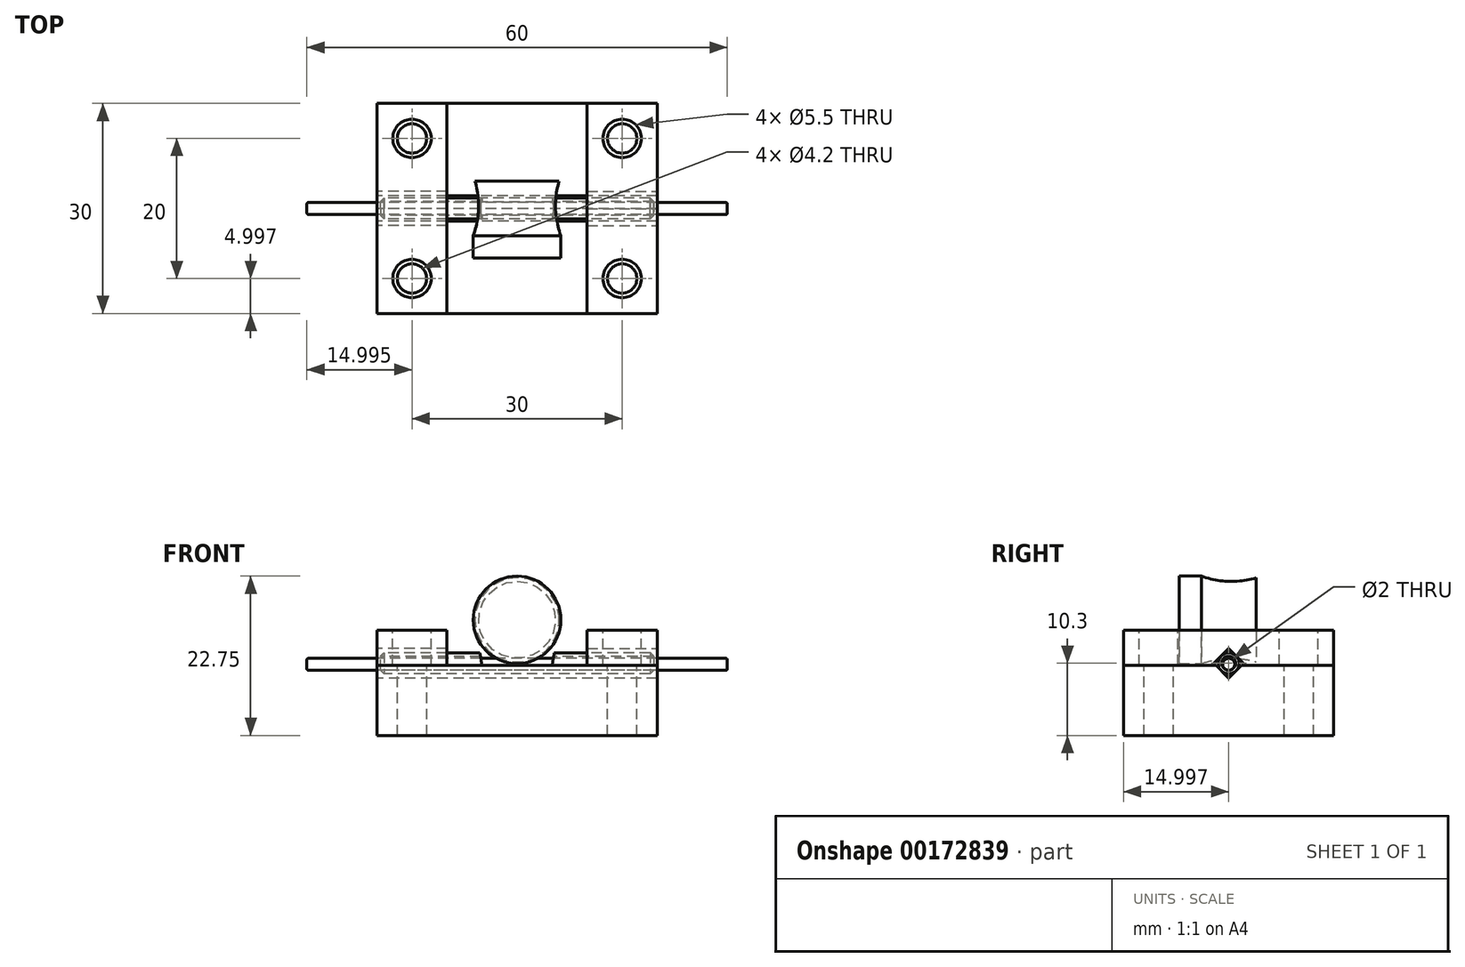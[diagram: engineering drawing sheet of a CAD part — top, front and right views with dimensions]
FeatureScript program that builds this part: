
annotation { "Feature Type Name" : "Feature", "Feature Type Description" : "" }
export const myFeature = defineFeature(function(context is Context, id is Id, definition is map)
    precondition{}
    {
        {
            var Q0;
            Q0=qCreatedBy(makeId("Top.planeOp"),FACE);
            var sketch = newSketch(context, id + "F0", { "sketchPlane" : qUnion([Q0])});
            skLineSegment(sketch, "E0.bottom", {"start": v(4.07, 8.16) * mm, "end": v(44.07, 8.16) * mm});
            skLineSegment(sketch, "E0.top", {"start": v(4.07, -21.84) * mm, "end": v(44.07, -21.84) * mm});
            skLineSegment(sketch, "E0.left", {"start": v(4.07, 8.16) * mm, "end": v(4.07, -21.84) * mm});
            skLineSegment(sketch, "E0.right", {"start": v(44.07, 8.16) * mm, "end": v(44.07, -21.84) * mm});
            skPoint(sketch, "E1", {"position": v(9.07, 3.16) * mm});
            skPoint(sketch, "E2", {"position": v(39.07, -16.84) * mm});
            skPoint(sketch, "E3", {"position": v(9.07, -16.84) * mm});
            skPoint(sketch, "E4", {"position": v(39.07, 3.16) * mm});
            skSolve(sketch);
        }
        {
            var Q0;
            Q0=makeQuery(id+"F0.imprint","IMPRINT",FACE,{"disambiguationData":[TD([[makeQuery(id+"F0.imprint","IMPRINT",EDGE,{"derivedFrom":sQuery(id+"F0.wireOp",EDGE,"E0.bottom")}),-1.0]])]});
            extrude(context, id + "F1", {"entities" : qUnion([Q0]), "depth" : 10 * mm});
        }
        {
            var Q0;
            Q0=makeQuery(id+"F1.opExtrude","CAP_FACE",FACE,{"disambiguationData":[OSD([sQuery(id+"F0.wireOp",EDGE,"E0.bottom"),sQuery(id+"F0.wireOp",EDGE,"E0.top"),sQuery(id+"F0.wireOp",EDGE,"E0.left"),sQuery(id+"F0.wireOp",EDGE,"E0.right")])],"isStart":false});
            var sketch = newSketch(context, id + "F2", { "sketchPlane" : qUnion([Q0])});
            skPoint(sketch, "E5", {"position": v(9.07, 3.16) * mm});
            skPoint(sketch, "E6", {"position": v(39.07, -16.84) * mm});
            skPoint(sketch, "E7", {"position": v(39.07, 3.16) * mm});
            skPoint(sketch, "E8", {"position": v(9.07, -16.84) * mm});
            skSolve(sketch);
        }
        {
            var Q0;
            Q0=makeQuery(id+"F1.opExtrude","SWEPT_FACE",FACE,{"disambiguationData":[OSD([sQuery(id+"F0.wireOp",EDGE,"E0.left")])]});
            var sketch = newSketch(context, id + "F3", { "sketchPlane" : qUnion([Q0])});
            skLineSegment(sketch, "E9", {"start": v(5.02, 10) * mm, "end": v(6.84, 8.18) * mm});
            skLineSegment(sketch, "E10", {"start": v(6.84, 8.18) * mm, "end": v(8.66, 10) * mm});
            skPoint(sketch, "E11", {"position": v(6.84, 10) * mm});
            skLineSegment(sketch, "E12", {"start": v(5.02, 10) * mm, "end": v(6.84, 10) * mm});
            skLineSegment(sketch, "E13", {"start": v(6.84, 10) * mm, "end": v(8.66, 10) * mm});
            skCircle(sketch, "E14", {"center": v(6.84, 10.3) * mm, "radius": 1.5 * mm});
            skLineSegment(sketch, "E15", {"start": v(5.34, 10.3) * mm, "end": v(8.34, 10.3) * mm});
            skSolve(sketch);
        }
        {
            var Q0;
            {var subQ0=sQuery(id+"F3.wireOp",EDGE,"E10");var subQ1=sQuery(id+"F3.wireOp",EDGE,"E9");var subQ2=makeQuery(id+"F3.imprint","INTERSECT",VERTEX,{"derivedFrom":[subQ1,subQ0]});Q0=makeQuery(id+"F3.imprint","IMPRINT",FACE,{"disambiguationData":[TD([[makeQuery(id+"F3.imprint","IMPRINT",EDGE,{"disambiguationData":[TD([[subQ2,1.0]])],"derivedFrom":subQ1}),1.0]])]});}
            var Q1;
            {var subQ3=sQuery(id+"F3.wireOp",EDGE,"E12");var subQ5=sQuery(id+"F3.wireOp",EDGE,"E13");var subQ6=makeQuery(id+"F3.imprint","INTERSECT",VERTEX,{"derivedFrom":[subQ3,subQ5]});Q1=makeQuery(id+"F3.imprint","IMPRINT",FACE,{"disambiguationData":[TD([[makeQuery(id+"F3.imprint","IMPRINT",EDGE,{"disambiguationData":[TD([[subQ6,1.0]])],"derivedFrom":subQ3}),-1.0]])]});}
            var Q2;
            {var subQ0=sQuery(id+"F3.wireOp",EDGE,"E12");var subQ3=sQuery(id+"F3.wireOp",EDGE,"E14");var subQ5=makeQuery(id+"F3.imprint","INTERSECT",VERTEX,{"derivedFrom":[subQ0,subQ3]});Q2=makeQuery(id+"F3.imprint","IMPRINT",FACE,{"disambiguationData":[TD([[makeQuery(id+"F3.imprint","IMPRINT",EDGE,{"disambiguationData":[TD([[subQ5,-1.0]])],"derivedFrom":subQ3}),-1.0]])]});}
            var Q3;
            {var subQ0=sQuery(id+"F3.wireOp",EDGE,"E13");var subQ3=sQuery(id+"F3.wireOp",EDGE,"E14");var subQ5=makeQuery(id+"F3.imprint","INTERSECT",VERTEX,{"derivedFrom":[subQ0,subQ3]});Q3=makeQuery(id+"F3.imprint","IMPRINT",FACE,{"disambiguationData":[TD([[makeQuery(id+"F3.imprint","IMPRINT",EDGE,{"disambiguationData":[TD([[subQ5,1.0]])],"derivedFrom":subQ3}),-1.0]])]});}
            extrude(context, id + "F4", {"entities" : qUnion([Q0, Q1, Q2, Q3]), "operationType" : NewBodyOperationType.REMOVE, "endBound" : BoundingType.UP_TO_NEXT, "oppositeDirection" : true, "depth" : 25 * mm});
        }
        {
            var Q0;
            Q0=sQuery(id+"F2.wireOp",VERTEX,"E5");
            var Q1;
            Q1=sQuery(id+"F2.wireOp",VERTEX,"E7");
            var Q2;
            Q2=sQuery(id+"F2.wireOp",VERTEX,"E6");
            var Q3;
            Q3=sQuery(id+"F2.wireOp",VERTEX,"E8");
            var Q4;
            Q4=makeQuery(id+"F1.opExtrude","SWEPT_BODY",BODY,{"disambiguationData":[OSD([sQuery(id+"F0.wireOp",EDGE,"E0.bottom"),sQuery(id+"F0.wireOp",EDGE,"E0.top"),sQuery(id+"F0.wireOp",EDGE,"E0.left"),sQuery(id+"F0.wireOp",EDGE,"E0.right")])]});
            hole(context, id + "F5", {"style" : HoleStyle.SIMPLE, "endStyle" : HoleEndStyle.THROUGH, "standardTappedOrClearance" : lookupTablePath({ "standard" : "ISO", "engagement" : "75%", "pitch" : "0.8 mm", "size" : "M5", "type" : "Tapped" }), "standardBlindInLast" : lookupTablePath({ "standard" : "ISO", "engagement" : "75%", "pitch" : "0.8 mm", "size" : "M5", "type" : "Tapped" }), "holeDiameter" : 4.2 * mm, "locations" : qUnion([Q0, Q1, Q2, Q3]), "scope" : qUnion([Q4]), "isTappedThrough" : true, "majorDiameter" : 5 * mm, "showTappedDepth" : true});
        }
        {
            var Q0;
            Q0=makeQuery(id+"F1.opExtrude","SWEPT_FACE",FACE,{"disambiguationData":[OSD([sQuery(id+"F0.wireOp",EDGE,"E0.left")])]});
            var sketch = newSketch(context, id + "F6", { "sketchPlane" : qUnion([Q0])});
            skLineSegment(sketch, "E16.bottom", {"start": v(-8.16, 10) * mm, "end": v(21.84, 10) * mm});
            skLineSegment(sketch, "E16.top", {"start": v(-8.16, 15) * mm, "end": v(21.84, 15) * mm});
            skLineSegment(sketch, "E16.left", {"start": v(-8.16, 10) * mm, "end": v(-8.16, 15) * mm});
            skLineSegment(sketch, "E16.right", {"start": v(21.84, 10) * mm, "end": v(21.84, 15) * mm});
            skCircle(sketch, "E17", {"center": v(6.84, 10.3) * mm, "radius": 1.5 * mm});
            skLineSegment(sketch, "E18", {"start": v(4.42, 10) * mm, "end": v(6.84, 12.42) * mm});
            skLineSegment(sketch, "E19", {"start": v(6.84, 12.42) * mm, "end": v(9.26, 10) * mm});
            skSolve(sketch);
        }
        {
            var Q0;
            Q0=makeQuery(id+"F6.imprint","IMPRINT",FACE,{"disambiguationData":[TD([[makeQuery(id+"F6.imprint","IMPRINT",EDGE,{"derivedFrom":sQuery(id+"F6.wireOp",EDGE,"E16.top")}),-1.0]])]});
            extrude(context, id + "F7", {"entities" : qUnion([Q0]), "oppositeDirection" : true, "depth" : 10 * mm});
        }
        {
            var Q0;
            Q0=makeQuery(id+"F1.opExtrude","SWEPT_FACE",FACE,{"disambiguationData":[OSD([sQuery(id+"F0.wireOp",EDGE,"E0.right")])]});
            var sketch = newSketch(context, id + "F8", { "sketchPlane" : qUnion([Q0])});
            skCircle(sketch, "E20", {"center": v(-6.84, 10.3) * mm, "radius": 1.5 * mm});
            skLineSegment(sketch, "E21", {"start": v(-9.26, 10) * mm, "end": v(-6.84, 12.42) * mm});
            skLineSegment(sketch, "E22", {"start": v(-6.84, 12.42) * mm, "end": v(-4.42, 10) * mm});
            skLineSegment(sketch, "E23.bottom", {"start": v(-21.84, 10) * mm, "end": v(8.16, 10) * mm});
            skLineSegment(sketch, "E23.top", {"start": v(-21.84, 15) * mm, "end": v(8.16, 15) * mm});
            skLineSegment(sketch, "E23.left", {"start": v(-21.84, 10) * mm, "end": v(-21.84, 15) * mm});
            skLineSegment(sketch, "E23.right", {"start": v(8.16, 10) * mm, "end": v(8.16, 15) * mm});
            skSolve(sketch);
        }
        {
            var Q0;
            Q0=makeQuery(id+"F8.imprint","IMPRINT",FACE,{"disambiguationData":[TD([[makeQuery(id+"F8.imprint","IMPRINT",EDGE,{"derivedFrom":sQuery(id+"F8.wireOp",EDGE,"E23.top")}),-1.0]])]});
            extrude(context, id + "F9", {"entities" : qUnion([Q0]), "oppositeDirection" : true, "depth" : 10 * mm});
        }
        {
            var Q0;
            Q0=makeQuery(id+"F7.opExtrude","SWEPT_FACE",FACE,{"disambiguationData":[OSD([sQuery(id+"F6.wireOp",EDGE,"E16.top")])]});
            var sketch = newSketch(context, id + "F10", { "sketchPlane" : qUnion([Q0])});
            skPoint(sketch, "E24", {"position": v(9.07, 3.16) * mm});
            skPoint(sketch, "E25", {"position": v(9.07, -16.84) * mm});
            skCircle(sketch, "E26", {"center": v(9.07, 3.16) * mm, "radius": 2.75 * mm});
            skCircle(sketch, "E27", {"center": v(9.07, -16.84) * mm, "radius": 2.75 * mm});
            skSolve(sketch);
        }
        {
            var Q0;
            Q0=makeQuery(id+"F10.imprint","IMPRINT",FACE,{"disambiguationData":[TD([[makeQuery(id+"F10.imprint","IMPRINT",EDGE,{"derivedFrom":sQuery(id+"F10.wireOp",EDGE,"E26")}),1.0]])]});
            var Q1;
            Q1=makeQuery(id+"F10.imprint","IMPRINT",FACE,{"disambiguationData":[TD([[makeQuery(id+"F10.imprint","IMPRINT",EDGE,{"derivedFrom":sQuery(id+"F10.wireOp",EDGE,"E27")}),1.0]])]});
            extrude(context, id + "F11", {"entities" : qUnion([Q0, Q1]), "operationType" : NewBodyOperationType.REMOVE, "endBound" : BoundingType.UP_TO_NEXT, "oppositeDirection" : true, "depth" : 25 * mm});
        }
        {
            var Q0;
            Q0=makeQuery(id+"F9.opExtrude","SWEPT_FACE",FACE,{"disambiguationData":[OSD([sQuery(id+"F8.wireOp",EDGE,"E23.top")])]});
            var sketch = newSketch(context, id + "F12", { "sketchPlane" : qUnion([Q0])});
            skCircle(sketch, "E28", {"center": v(39.07, 3.16) * mm, "radius": 2.75 * mm});
            skCircle(sketch, "E29", {"center": v(39.07, -16.84) * mm, "radius": 2.75 * mm});
            skSolve(sketch);
        }
        {
            var Q0;
            Q0=makeQuery(id+"F12.imprint","IMPRINT",FACE,{"disambiguationData":[TD([[makeQuery(id+"F12.imprint","IMPRINT",EDGE,{"derivedFrom":sQuery(id+"F12.wireOp",EDGE,"E28")}),1.0]])]});
            var Q1;
            Q1=makeQuery(id+"F12.imprint","IMPRINT",FACE,{"disambiguationData":[TD([[makeQuery(id+"F12.imprint","IMPRINT",EDGE,{"derivedFrom":sQuery(id+"F12.wireOp",EDGE,"E29")}),1.0]])]});
            extrude(context, id + "F13", {"entities" : qUnion([Q0, Q1]), "operationType" : NewBodyOperationType.REMOVE, "endBound" : BoundingType.UP_TO_NEXT, "oppositeDirection" : true, "depth" : 25 * mm});
        }
        {
            var Q0;
            Q0=makeQuery(id+"F7.opExtrude","CAP_FACE",FACE,{"disambiguationData":[OSD([sQuery(id+"F6.wireOp",EDGE,"E16.bottom"),sQuery(id+"F6.wireOp",EDGE,"E16.top"),sQuery(id+"F6.wireOp",EDGE,"E16.left"),sQuery(id+"F6.wireOp",EDGE,"E16.right"),sQuery(id+"F6.wireOp",EDGE,"E18"),sQuery(id+"F6.wireOp",EDGE,"E19")])],"isStart":true});
            cPlane(context, id + "F14", {"entities" : qUnion([Q0]), "cplaneType" : CPlaneType.OFFSET, "offset" : 0 * mm, "width" : 150 * mm, "height" : 150 * mm});
        }
        {
            var Q0;
            Q0=qCreatedBy(id+"F14.planeOp",FACE);
            var sketch = newSketch(context, id + "F15", { "sketchPlane" : qUnion([Q0])});
            skCircle(sketch, "E30", {"center": v(6.84, 10.3) * mm, "radius": 1.5 * mm});
            skCircle(sketch, "E31", {"center": v(6.84, 10.3) * mm, "radius": 1 * mm});
            skSolve(sketch);
        }
        {
            var Q0;
            Q0=makeQuery(id+"F15.imprint","IMPRINT",FACE,{"disambiguationData":[TD([[makeQuery(id+"F15.imprint","IMPRINT",EDGE,{"derivedFrom":sQuery(id+"F15.wireOp",EDGE,"E30")}),1.0]])]});
            extrude(context, id + "F16", {"entities" : qUnion([Q0]), "oppositeDirection" : true, "depth" : 40 * mm});
        }
        {
            var Q0;
            Q0=makeQuery(id+"F1.opExtrude","SWEPT_FACE",FACE,{"disambiguationData":[OSD([sQuery(id+"F0.wireOp",EDGE,"E0.top")])]});
            var sketch = newSketch(context, id + "F17", { "sketchPlane" : qUnion([Q0])});
            skPoint(sketch, "E32", {"position": v(24.07, 10) * mm});
            skLineSegment(sketch, "E33.bottom", {"start": v(19.07, 15.8) * mm, "end": v(29.07, 15.8) * mm});
            skLineSegment(sketch, "E33.top", {"start": v(19.07, 10) * mm, "end": v(29.07, 10) * mm});
            skLineSegment(sketch, "E33.left", {"start": v(19.07, 15.8) * mm, "end": v(19.07, 10) * mm});
            skLineSegment(sketch, "E33.right", {"start": v(29.07, 15.8) * mm, "end": v(29.07, 10) * mm});
            skPoint(sketch, "E34", {"position": v(24.07, 15.8) * mm});
            skLineSegment(sketch, "E35", {"start": v(19.07, 10) * mm, "end": v(18.07, 15.8) * mm});
            skLineSegment(sketch, "E36", {"start": v(18.07, 15.8) * mm, "end": v(19.07, 15.8) * mm});
            skLineSegment(sketch, "E37", {"start": v(29.07, 15.8) * mm, "end": v(30.07, 15.8) * mm});
            skLineSegment(sketch, "E38", {"start": v(30.07, 15.8) * mm, "end": v(29.07, 10) * mm});
            skSolve(sketch);
        }
        {
            var Q0;
            Q0=makeQuery(id+"F17.imprint","IMPRINT",FACE,{"disambiguationData":[TD([[makeQuery(id+"F17.imprint","IMPRINT",EDGE,{"derivedFrom":sQuery(id+"F17.wireOp",EDGE,"E33.bottom")}),-1.0]])]});
            var Q1;
            Q1=makeQuery(id+"F17.imprint","IMPRINT",FACE,{"disambiguationData":[TD([[makeQuery(id+"F17.imprint","IMPRINT",EDGE,{"derivedFrom":sQuery(id+"F17.wireOp",EDGE,"E33.left")}),-1.0]])]});
            var Q2;
            Q2=makeQuery(id+"F17.imprint","IMPRINT",FACE,{"disambiguationData":[TD([[makeQuery(id+"F17.imprint","IMPRINT",EDGE,{"derivedFrom":sQuery(id+"F17.wireOp",EDGE,"E33.right")}),1.0]])]});
            extrude(context, id + "F18", {"entities" : qUnion([Q0, Q1, Q2]), "operationType" : NewBodyOperationType.REMOVE, "oppositeDirection" : true, "depth" : 25 * mm});
        }
        {
            var Q0;
            Q0=makeQuery(id+"F16.opExtrude","CAP_EDGE",EDGE,{"disambiguationData":[OSD([sQuery(id+"F15.wireOp",EDGE,"E30")])],"isStart":true});
            var Q1;
            Q1=makeQuery(id+"F16.opExtrude","CAP_EDGE",EDGE,{"disambiguationData":[OSD([sQuery(id+"F15.wireOp",EDGE,"E30")])],"isStart":false});
            chamfer(context, id + "F19", {"entities" : qUnion([Q0, Q1]), "width" : 1 * mm, "tangentPropagation" : true});
        }
        {
            var Q0;
            Q0=qCreatedBy(id+"F14.planeOp",FACE);
            var sketch = newSketch(context, id + "F20", { "sketchPlane" : qUnion([Q0])});
            skCircle(sketch, "E39", {"center": v(6.84, 10.15) * mm, "radius": 0.85 * mm});
            skSolve(sketch);
        }
        {
            var Q0;
            Q0=makeQuery(id+"F20.imprint","IMPRINT",FACE,{"disambiguationData":[TD([[makeQuery(id+"F20.imprint","IMPRINT",EDGE,{"derivedFrom":sQuery(id+"F20.wireOp",EDGE,"E39")}),1.0]])]});
            extrude(context, id + "F21", {"entities" : qUnion([Q0]), "oppositeDirection" : true, "depth" : 50 * mm});
        }
        {
            var Q0;
            Q0=makeQuery(id+"F21.opExtrude","CAP_FACE",FACE,{"disambiguationData":[OSD([sQuery(id+"F20.wireOp",EDGE,"E39")])],"isStart":true});
            extrude(context, id + "F22", {"entities" : qUnion([Q0]), "operationType" : NewBodyOperationType.ADD, "depth" : 10 * mm});
        }
        {
            var Q0;
            Q0=makeQuery(id+"F1.opExtrude","SWEPT_FACE",FACE,{"disambiguationData":[OSD([sQuery(id+"F0.wireOp",EDGE,"E0.left")])]});
            cPlane(context, id + "F23", {"entities" : qUnion([Q0]), "cplaneType" : CPlaneType.OFFSET, "offset" : 20 * mm, "oppositeDirection" : true, "width" : 150 * mm, "height" : 150 * mm});
        }
        {
            var Q0;
            Q0=qCreatedBy(id+"F23.planeOp",FACE);
            var sketch = newSketch(context, id + "F24", { "sketchPlane" : qUnion([Q0])});
            skLineSegment(sketch, "E40", {"start": v(13.92, 22.75) * mm, "end": v(10.72, 22.75) * mm});
            skArc(sketch, "E41", {"start": v(2.92, 22.5) * mm, "mid": v(6.84, 22) * mm, "end": v(10.72, 22.75) * mm});
            skPoint(sketch, "E42", {"position": v(6.84, 22) * mm});
            skPoint(sketch, "E43", {"position": v(2.92, 16.5) * mm});
            skPoint(sketch, "E44", {"position": v(13.92, 16.5) * mm});
            skLineSegment(sketch, "E45", {"start": v(2.92, 16.5) * mm, "end": v(13.92, 16.5) * mm});
            skLineSegment(sketch, "E46", {"start": v(2.92, 22.5) * mm, "end": v(2.92, 16.5) * mm});
            skLineSegment(sketch, "E47", {"start": v(13.92, 16.5) * mm, "end": v(13.92, 22.75) * mm});
            skArc(sketch, "E48.0", {"start": v(2.71, 21.78) * mm, "mid": v(6.87, 21.25) * mm, "end": v(10.98, 22.05) * mm});
            skSolve(sketch);
        }
        {
            var Q0;
            Q0=makeQuery(id+"F24.imprint","IMPRINT",FACE,{"disambiguationData":[TD([[makeQuery(id+"F24.imprint","IMPRINT",EDGE,{"derivedFrom":sQuery(id+"F24.wireOp",EDGE,"E40")}),1.0]])]});
            var Q1;
            Q1=sQuery(id+"F24.wireOp",EDGE,"E45");
            revolve(context, id + "F25", {"entities" : qUnion([Q0]), "axis" : qUnion([Q1]), "revolveType" : RevolveType.FULL});
        }
        {
            var Q0;
            Q0=makeQuery(id+"F22.opExtrude","CAP_EDGE",EDGE,{"disambiguationData":[OSD([sQuery(id+"F20.wireOp",EDGE,"E39")])],"isStart":false});
            var Q1;
            Q1=makeQuery(id+"F21.opExtrude","CAP_EDGE",EDGE,{"disambiguationData":[OSD([sQuery(id+"F20.wireOp",EDGE,"E39")])],"isStart":false});
            fillet(context, id + "F26", {"entities" : qUnion([Q0, Q1]), "radius" : 0.2 * mm, "tangentPropagation" : true, "allowEdgeOverflow" : false});
        }
    });
